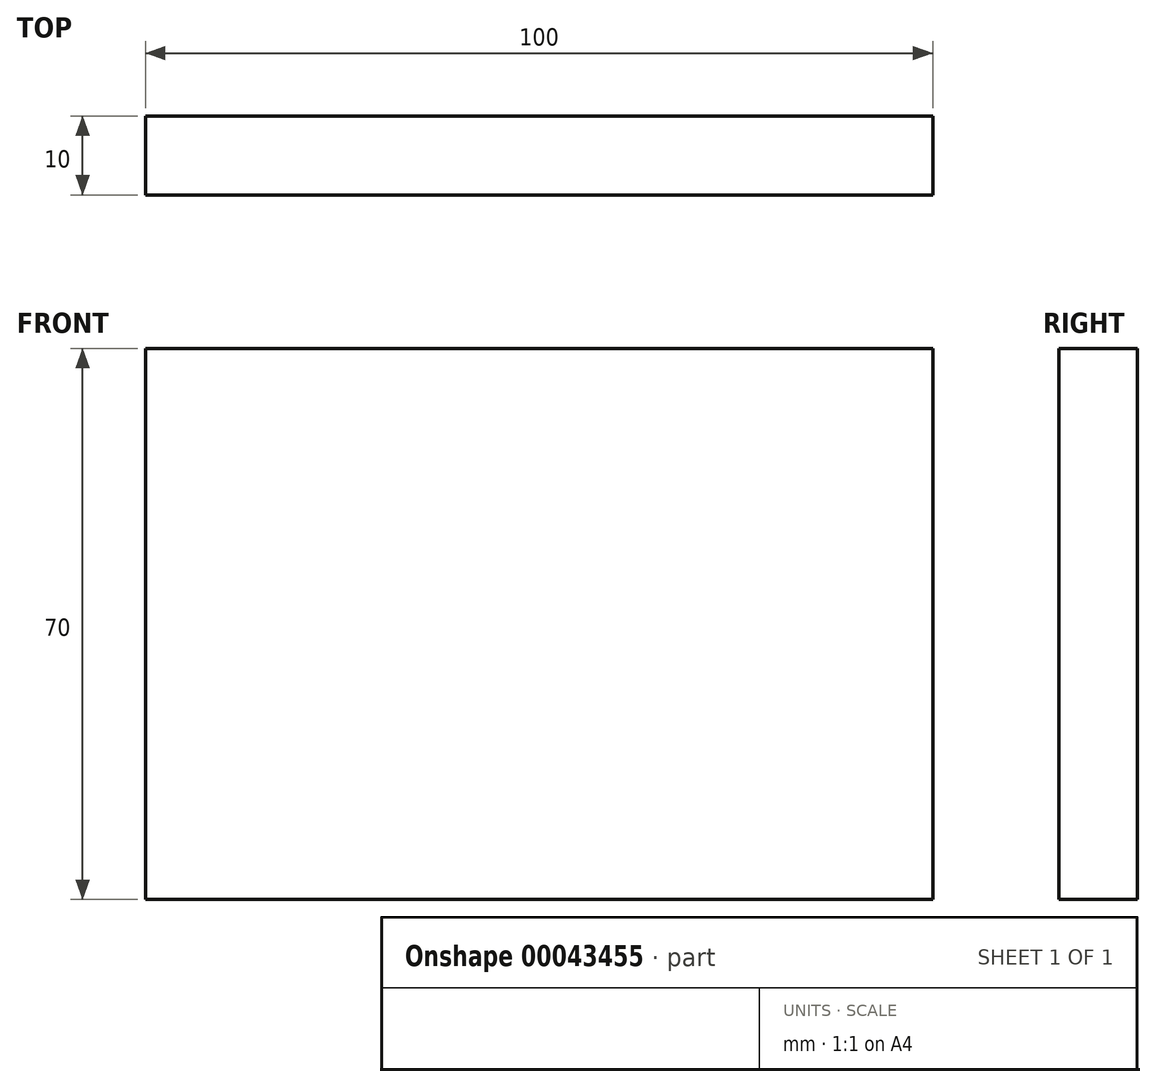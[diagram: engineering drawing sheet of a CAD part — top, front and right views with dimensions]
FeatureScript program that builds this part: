
annotation { "Feature Type Name" : "Feature", "Feature Type Description" : "" }
export const myFeature = defineFeature(function(context is Context, id is Id, definition is map)
    precondition{}
    {
        {
            var Q0;
            Q0=qCreatedBy(makeId("Front.planeOp"),FACE);
            var sketch = newSketch(context, id + "F0", { "sketchPlane" : qUnion([Q0])});
            skLineSegment(sketch, "E0.rect.bottom", {"start": v(50, 35) * mm, "end": v(-50, 35) * mm});
            skLineSegment(sketch, "E0.rect.top", {"start": v(50, -35) * mm, "end": v(-50, -35) * mm});
            skLineSegment(sketch, "E0.rect.left", {"start": v(50, 35) * mm, "end": v(50, -35) * mm});
            skLineSegment(sketch, "E0.rect.right", {"start": v(-50, 35) * mm, "end": v(-50, -35) * mm});
            skPoint(sketch, "E0.rect.middle", {"position": v(0, 0) * mm});
            skSolve(sketch);
        }
        {
            var Q0;
            Q0=makeQuery(id+"F0.imprint","IMPRINT",FACE,{"disambiguationData":[TD([[makeQuery(id+"F0.imprint","IMPRINT",EDGE,{"derivedFrom":sQuery(id+"F0.wireOp",EDGE,"E0.rect.bottom")}),1.0]])]});
            extrude(context, id + "F1", {"entities" : qUnion([Q0]), "depth" : 10 * mm});
        }
    });
